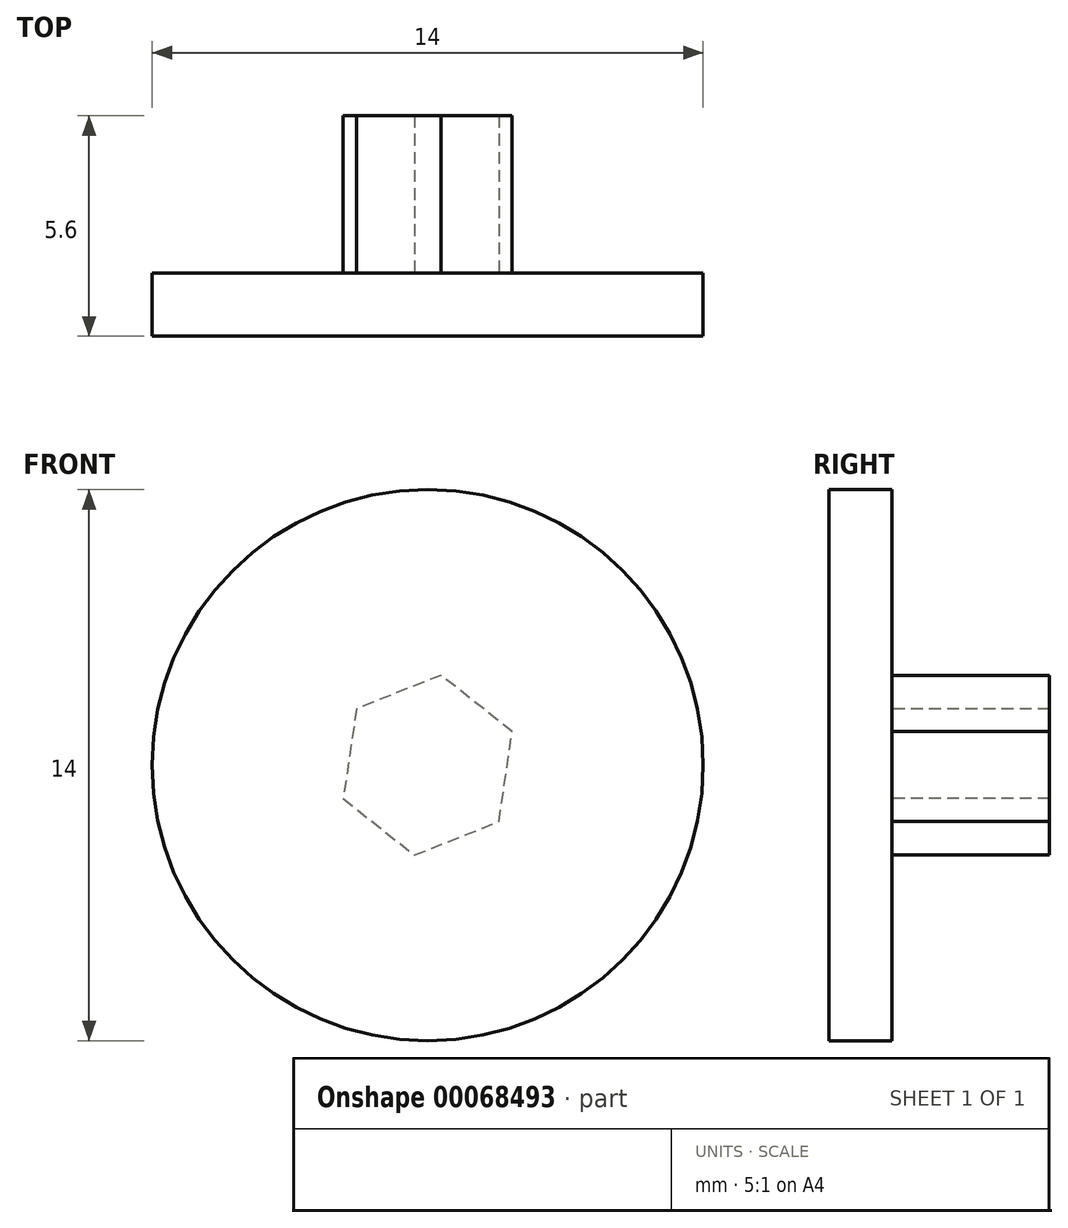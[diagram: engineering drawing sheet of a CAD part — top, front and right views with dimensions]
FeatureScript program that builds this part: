
annotation { "Feature Type Name" : "Feature", "Feature Type Description" : "" }
export const myFeature = defineFeature(function(context is Context, id is Id, definition is map)
    precondition{}
    {
        {
            var Q0;
            Q0=qCreatedBy(makeId("Front.planeOp"),FACE);
            var sketch = newSketch(context, id + "F0", { "sketchPlane" : qUnion([Q0])});
            skCircle(sketch, "E0", {"center": v(0, 0) * mm, "radius": 7 * mm});
            skSolve(sketch);
        }
        {
            var Q0;
            Q0 = qSketchRegion(id + "F0", true);
            extrude(context, id + "F1", {"entities" : qUnion([Q0]), "depth" : 1.6 * mm});
        }
        {
            var Q0;
            Q0=makeQuery(id+"F1.opExtrude","CAP_FACE",FACE,{"disambiguationData":[OSD([sQuery(id+"F0.wireOp",EDGE,"E0")])],"isStart":true});
            var sketch = newSketch(context, id + "F2", { "sketchPlane" : qUnion([Q0])});
            skCircle(sketch, "E1.cCircle", {"center": v(0, 0) * mm, "radius": 2 * mm, "construction": true});
            skLineSegment(sketch, "E1.0", {"start": v(0.34, -2.28) * mm, "end": v(-1.81, -1.43) * mm});
            skLineSegment(sketch, "E1.1", {"start": v(-1.81, -1.43) * mm, "end": v(-2.15, 0.85) * mm});
            skLineSegment(sketch, "E1.2", {"start": v(-2.15, 0.85) * mm, "end": v(-0.34, 2.28) * mm});
            skLineSegment(sketch, "E1.3", {"start": v(-0.34, 2.28) * mm, "end": v(1.81, 1.43) * mm});
            skLineSegment(sketch, "E1.4", {"start": v(1.81, 1.43) * mm, "end": v(2.15, -0.85) * mm});
            skLineSegment(sketch, "E1.5", {"start": v(2.15, -0.85) * mm, "end": v(0.34, -2.28) * mm});
            skPoint(sketch, "E1.0.midPoint", {"position": v(-0.74, -1.86) * mm});
            skSolve(sketch);
        }
        {
            var Q0;
            Q0=makeQuery(id+"F2.imprint","IMPRINT",FACE,{"disambiguationData":[TD([[makeQuery(id+"F2.imprint","IMPRINT",EDGE,{"derivedFrom":sQuery(id+"F2.wireOp",EDGE,"E1.0")}),-1.0]])]});
            extrude(context, id + "F3", {"entities" : qUnion([Q0]), "operationType" : NewBodyOperationType.ADD, "depth" : 4 * mm});
        }
    });
